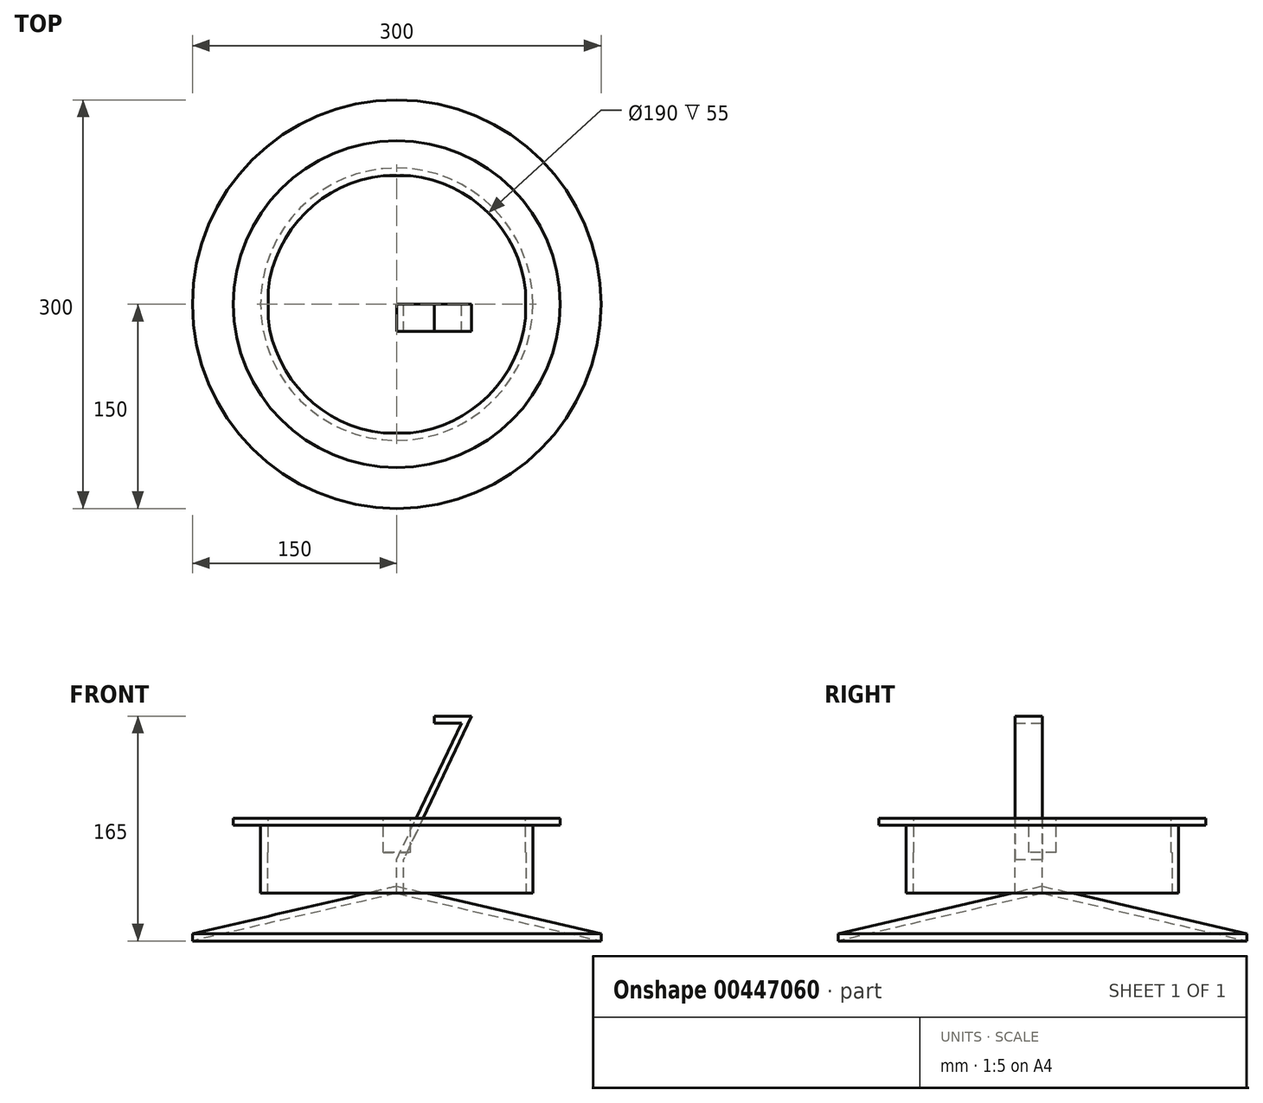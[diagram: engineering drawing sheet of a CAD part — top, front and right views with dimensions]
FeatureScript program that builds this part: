
annotation { "Feature Type Name" : "Feature", "Feature Type Description" : "" }
export const myFeature = defineFeature(function(context is Context, id is Id, definition is map)
    precondition{}
    {
        {
            var Q0;
            Q0=qCreatedBy(makeId("Front.planeOp"),FACE);
            var sketch = newSketch(context, id + "F0", { "sketchPlane" : qUnion([Q0])});
            skLineSegment(sketch, "E0", {"start": v(0, 5.13) * mm, "end": v(150, -29.87) * mm});
            skLineSegment(sketch, "E1", {"start": v(150, -29.87) * mm, "end": v(150, -35) * mm});
            skLineSegment(sketch, "E2", {"start": v(150, -35) * mm, "end": v(0, 0) * mm});
            skLineSegment(sketch, "E3", {"start": v(0, 0) * mm, "end": v(0, 5.13) * mm});
            skSolve(sketch);
        }
        {
            var Q0;
            Q0=qCreatedBy(makeId("Front.planeOp"),FACE);
            var sketch = newSketch(context, id + "F1", { "sketchPlane" : qUnion([Q0])});
            skLineSegment(sketch, "E4", {"start": v(0, 0) * mm, "end": v(0, 38.88) * mm, "construction": true});
            skSolve(sketch);
        }
        {
            var Q0;
            Q0=makeQuery(id+"F0.imprint","IMPRINT",FACE,{"disambiguationData":[TD([[makeQuery(id+"F0.imprint","IMPRINT",EDGE,{"derivedFrom":sQuery(id+"F0.wireOp",EDGE,"E0")}),-1.0]])]});
            var Q1;
            Q1=sQuery(id+"F1.wireOp",EDGE,"E4");
            revolve(context, id + "F2", {"entities" : qUnion([Q0]), "axis" : qUnion([Q1]), "revolveType" : RevolveType.FULL});
        }
        {
            var Q0;
            Q0=qCreatedBy(makeId("Top.planeOp"),FACE);
            var sketch = newSketch(context, id + "F3", { "sketchPlane" : qUnion([Q0])});
            skCircle(sketch, "E5", {"center": v(0, 0) * mm, "radius": 100 * mm});
            skCircle(sketch, "E6", {"center": v(0, 0) * mm, "radius": 95 * mm});
            skSolve(sketch);
        }
        {
            var Q0;
            Q0=makeQuery(id+"F3.imprint","IMPRINT",FACE,{"disambiguationData":[TD([[makeQuery(id+"F3.imprint","IMPRINT",EDGE,{"derivedFrom":sQuery(id+"F3.wireOp",EDGE,"E5")}),1.0]])]});
            extrude(context, id + "F4", {"entities" : qUnion([Q0]), "depth" : 50 * mm, "offsetDistance" : 25 * mm});
        }
        {
            var Q0;
            Q0=makeQuery(id+"F4.opExtrude","CAP_FACE",FACE,{"disambiguationData":[OSD([sQuery(id+"F3.wireOp",EDGE,"E5"),sQuery(id+"F3.wireOp",EDGE,"E6")])],"isStart":false});
            var sketch = newSketch(context, id + "F5", { "sketchPlane" : qUnion([Q0])});
            skCircle(sketch, "E7", {"center": v(0, 0) * mm, "radius": 120 * mm});
            skSolve(sketch);
        }
        {
            var Q0;
            Q0=makeQuery(id+"F5.imprint","IMPRINT",FACE,{"disambiguationData":[TD([[makeQuery(id+"F5.imprint","IMPRINT",EDGE,{"derivedFrom":sQuery(id+"F5.wireOp",EDGE,"E7")}),1.0]])]});
            var Q1;
            Q1=makeQuery(id+"F5.imprint","IMPRINT",FACE,{"disambiguationData":[TD([[makeQuery(id+"F5.imprint","IMPRINT",EDGE,{"derivedFrom":makeQuery(id+"F4.opExtrude","CAP_EDGE",EDGE,{"disambiguationData":[OSD([sQuery(id+"F3.wireOp",EDGE,"E5")])],"isStart":false})}),1.0]])]});
            extrude(context, id + "F6", {"entities" : qUnion([Q0, Q1]), "operationType" : NewBodyOperationType.ADD, "depth" : 5 * mm, "offsetDistance" : 25 * mm});
        }
        {
            var Q0;
            Q0=makeQuery(id+"F6.opExtrude","CAP_FACE",FACE,{"disambiguationData":[OSD([sQuery(id+"F3.wireOp",EDGE,"E6"),sQuery(id+"F5.wireOp",EDGE,"E7")])],"isStart":false});
            var sketch = newSketch(context, id + "F7", { "sketchPlane" : qUnion([Q0])});
            skLineSegment(sketch, "E8.bottom", {"start": v(-10, 99.47) * mm, "end": v(10, 99.47) * mm});
            skLineSegment(sketch, "E8.top", {"start": v(-10, 94.47) * mm, "end": v(10, 94.47) * mm});
            skLineSegment(sketch, "E8.left", {"start": v(-10, 99.47) * mm, "end": v(-10, 94.47) * mm});
            skLineSegment(sketch, "E8.right", {"start": v(10, 99.47) * mm, "end": v(10, 94.47) * mm});
            skLineSegment(sketch, "E9.bottom", {"start": v(99.47, 10) * mm, "end": v(94.47, 10) * mm});
            skLineSegment(sketch, "E9.top", {"start": v(99.47, -10) * mm, "end": v(94.47, -10) * mm});
            skLineSegment(sketch, "E9.left", {"start": v(99.47, 10) * mm, "end": v(99.47, -10) * mm});
            skLineSegment(sketch, "E9.right", {"start": v(94.47, 10) * mm, "end": v(94.47, -10) * mm});
            skLineSegment(sketch, "E10.bottom", {"start": v(-10, -94.47) * mm, "end": v(10, -94.47) * mm});
            skLineSegment(sketch, "E10.top", {"start": v(-10, -99.47) * mm, "end": v(10, -99.47) * mm});
            skLineSegment(sketch, "E10.left", {"start": v(-10, -94.47) * mm, "end": v(-10, -99.47) * mm});
            skLineSegment(sketch, "E10.right", {"start": v(10, -94.47) * mm, "end": v(10, -99.47) * mm});
            skLineSegment(sketch, "E11.bottom", {"start": v(-99.47, 10) * mm, "end": v(-94.47, 10) * mm});
            skLineSegment(sketch, "E11.top", {"start": v(-99.47, -10) * mm, "end": v(-94.47, -10) * mm});
            skLineSegment(sketch, "E11.left", {"start": v(-99.47, 10) * mm, "end": v(-99.47, -10) * mm});
            skLineSegment(sketch, "E11.right", {"start": v(-94.47, 10) * mm, "end": v(-94.47, -10) * mm});
            skSolve(sketch);
        }
        {
            var Q0;
            {var subQ0=sQuery(id+"F7.wireOp",EDGE,"E11.right");Q0=makeQuery(id+"F7.imprint","IMPRINT",FACE,{"disambiguationData":[TD([[makeQuery(id+"F7.imprint","IMPRINT",EDGE,{"derivedFrom":subQ0}),-1.0]])]});}
            var Q1;
            {var subQ0=sQuery(id+"F7.wireOp",EDGE,"E11.bottom");Q1=makeQuery(id+"F7.imprint","IMPRINT",FACE,{"disambiguationData":[TD([[makeQuery(id+"F7.imprint","IMPRINT",EDGE,{"derivedFrom":subQ0}),-1.0]])]});}
            var Q2;
            {var subQ0=sQuery(id+"F7.wireOp",EDGE,"E10.bottom");Q2=makeQuery(id+"F7.imprint","IMPRINT",FACE,{"disambiguationData":[TD([[makeQuery(id+"F7.imprint","IMPRINT",EDGE,{"derivedFrom":subQ0}),-1.0]])]});}
            var Q3;
            Q3=makeQuery(id+"F7.imprint","IMPRINT",FACE,{"disambiguationData":[TD([[makeQuery(id+"F7.imprint","IMPRINT",EDGE,{"derivedFrom":sQuery(id+"F7.wireOp",EDGE,"E10.top")}),1.0]])]});
            var Q4;
            {var subQ0=sQuery(id+"F7.wireOp",EDGE,"E9.right");Q4=makeQuery(id+"F7.imprint","IMPRINT",FACE,{"disambiguationData":[TD([[makeQuery(id+"F7.imprint","IMPRINT",EDGE,{"derivedFrom":subQ0}),1.0]])]});}
            var Q5;
            {var subQ0=sQuery(id+"F7.wireOp",EDGE,"E9.bottom");Q5=makeQuery(id+"F7.imprint","IMPRINT",FACE,{"disambiguationData":[TD([[makeQuery(id+"F7.imprint","IMPRINT",EDGE,{"derivedFrom":subQ0}),1.0]])]});}
            var Q6;
            Q6=makeQuery(id+"F7.imprint","IMPRINT",FACE,{"disambiguationData":[TD([[makeQuery(id+"F7.imprint","IMPRINT",EDGE,{"derivedFrom":sQuery(id+"F7.wireOp",EDGE,"E8.bottom")}),-1.0]])]});
            var Q7;
            {var subQ0=sQuery(id+"F7.wireOp",EDGE,"E8.top");Q7=makeQuery(id+"F7.imprint","IMPRINT",FACE,{"disambiguationData":[TD([[makeQuery(id+"F7.imprint","IMPRINT",EDGE,{"derivedFrom":subQ0}),1.0]])]});}
            extrude(context, id + "F8", {"entities" : qUnion([Q0, Q1, Q2, Q3, Q4, Q5, Q6, Q7]), "operationType" : NewBodyOperationType.ADD, "oppositeDirection" : true, "depth" : 25 * mm, "offsetDistance" : 25 * mm});
        }
        {
            var Q0;
            Q0=qCreatedBy(makeId("Front.planeOp"),FACE);
            var sketch = newSketch(context, id + "F9", { "sketchPlane" : qUnion([Q0])});
            skLineSegment(sketch, "E12", {"start": v(0, 0) * mm, "end": v(0, 25) * mm});
            skLineSegment(sketch, "E13", {"start": v(0, 0) * mm, "end": v(5, 0) * mm});
            skLineSegment(sketch, "E14", {"start": v(5, 0) * mm, "end": v(5, 25) * mm});
            skLineSegment(sketch, "E15", {"start": v(0, 25) * mm, "end": v(47.62, 125) * mm});
            skLineSegment(sketch, "E16", {"start": v(47.62, 125) * mm, "end": v(27.62, 125) * mm});
            skLineSegment(sketch, "E17", {"start": v(27.62, 125) * mm, "end": v(27.62, 130) * mm});
            skLineSegment(sketch, "E18", {"start": v(27.62, 130) * mm, "end": v(55, 130) * mm});
            skLineSegment(sketch, "E19", {"start": v(55, 130) * mm, "end": v(5, 25) * mm});
            skSolve(sketch);
        }
        {
            var Q0;
            Q0=makeQuery(id+"F9.imprint","IMPRINT",FACE,{"disambiguationData":[TD([[makeQuery(id+"F9.imprint","IMPRINT",EDGE,{"derivedFrom":sQuery(id+"F9.wireOp",EDGE,"E12")}),-1.0]])]});
            extrude(context, id + "F10", {"entities" : qUnion([Q0]), "depth" : 20 * mm, "offsetDistance" : 25 * mm});
        }
    });
